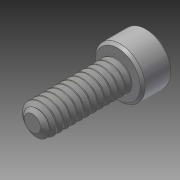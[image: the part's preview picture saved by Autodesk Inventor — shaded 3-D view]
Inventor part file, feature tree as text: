
AUTODESK INVENTOR PART (.ipt)
format: ipt  version: 2014 SP1 (Build 180222100, 222)  size: 584,192 bytes
history: native  units: in
note: dims shown in document units (in); Inventor stores cm internally (conversion verified against a paired STEP export)
features: chamfer x1, other x1, imported_body x1
ambient origin geometry x8: Origin, YZ Plane, XZ Plane, XY Plane, X Axis, Y Axis, Z Axis, Center Point
bodies: Body1 (feature_tree)
feature tree (3):
  chamfer  "Chamfer1"  [1 undecoded]
  other  "91251A107_91251A107.ipt1"
  imported_body  "Base1"
note: 1 required parameter value undecoded (feature->parameter linkage not recoverable at this tier; creation-order binding heuristic only, values carry confidence <= 0.55)
